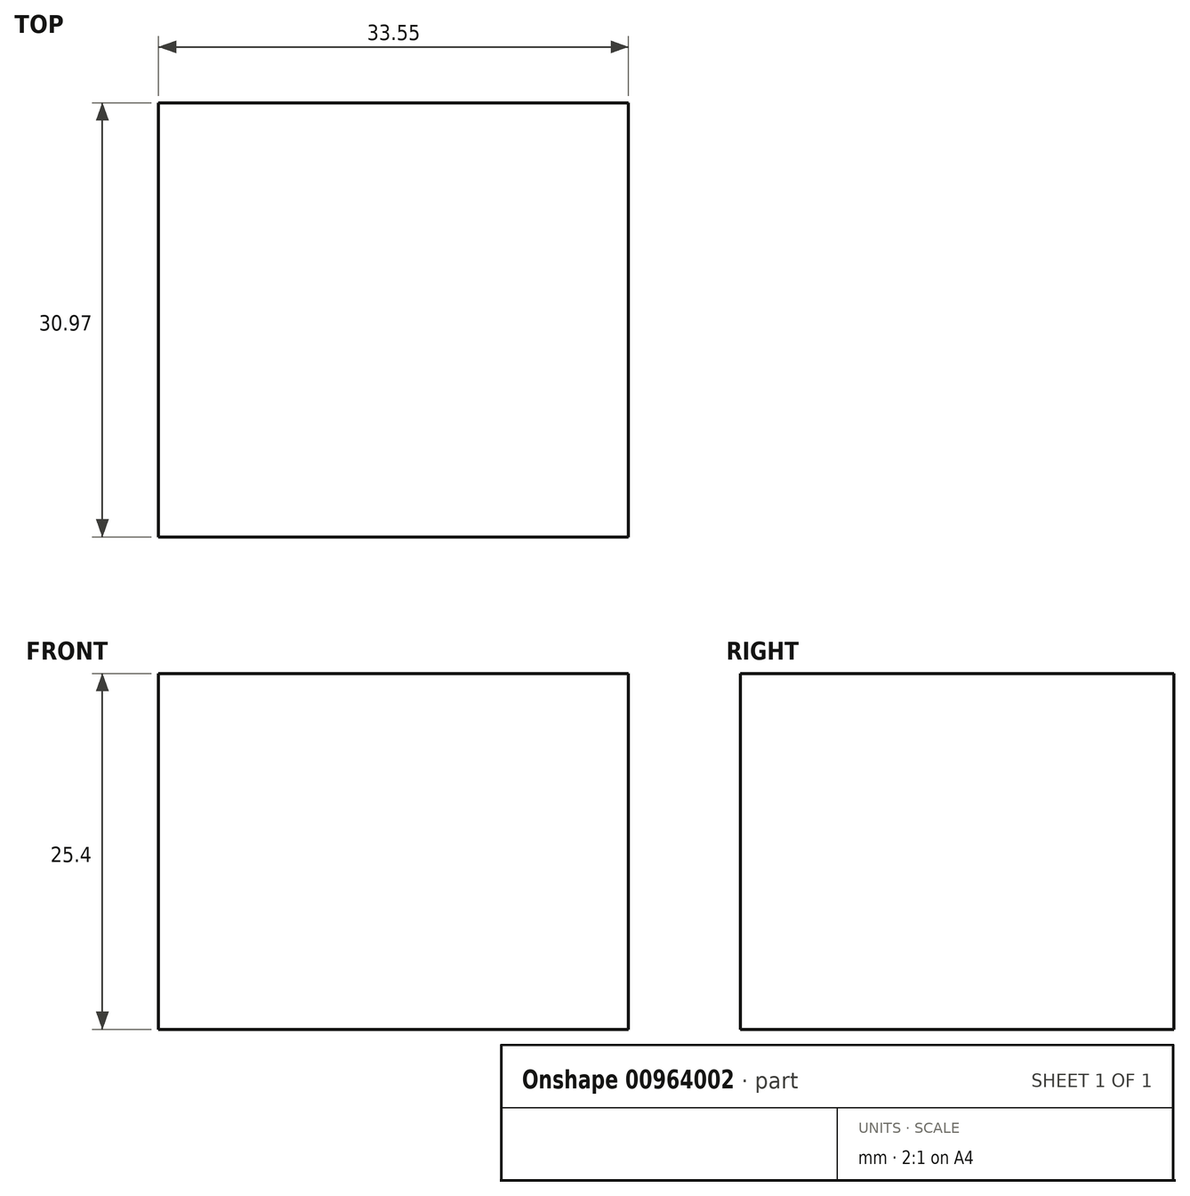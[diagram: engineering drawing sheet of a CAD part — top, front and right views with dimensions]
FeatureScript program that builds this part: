
annotation { "Feature Type Name" : "Feature", "Feature Type Description" : "" }
export const myFeature = defineFeature(function(context is Context, id is Id, definition is map)
    precondition{}
    {
        {
            var Q0;
            Q0=qCreatedBy(makeId("Top.planeOp"),FACE);
            var sketch = newSketch(context, id + "F0", { "sketchPlane" : qUnion([Q0])});
            skLineSegment(sketch, "E0.bottom", {"start": v(-13.64, 16.5) * mm, "end": v(19.91, 16.5) * mm});
            skLineSegment(sketch, "E0.top", {"start": v(-13.64, -14.47) * mm, "end": v(19.91, -14.47) * mm});
            skLineSegment(sketch, "E0.left", {"start": v(-13.64, 16.5) * mm, "end": v(-13.64, -14.47) * mm});
            skLineSegment(sketch, "E0.right", {"start": v(19.91, 16.5) * mm, "end": v(19.91, -14.47) * mm});
            skSolve(sketch);
        }
        {
            var Q0;
            Q0 = qSketchRegion(id + "F0", true);
            extrude(context, id + "F1", {"entities" : qUnion([Q0]), "depth" : 25.4 * mm, "offsetDistance" : 25.4 * mm});
        }
    });
